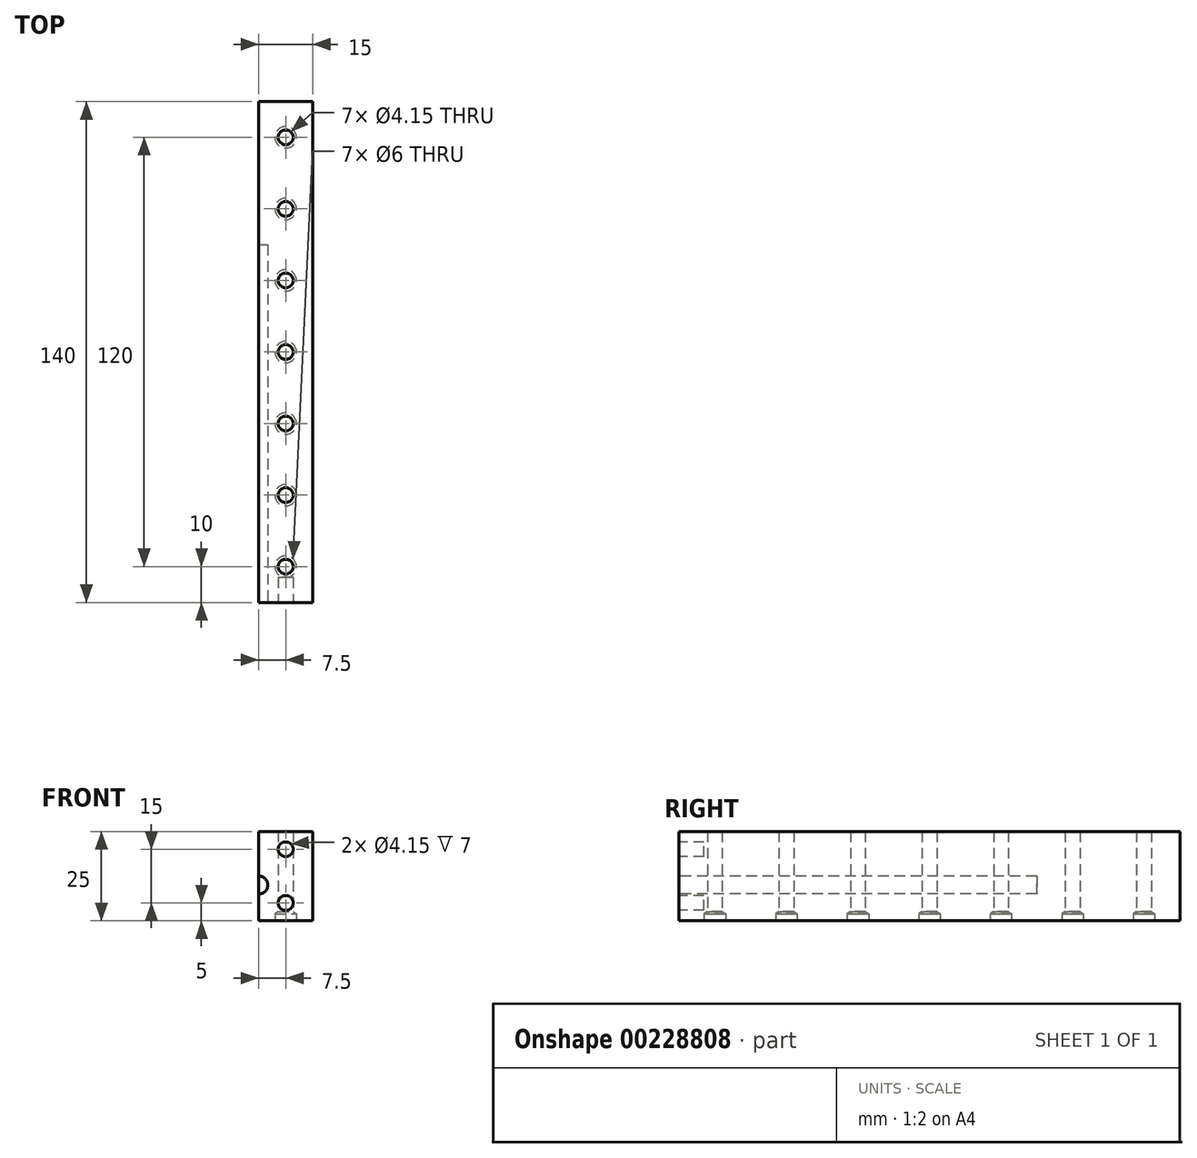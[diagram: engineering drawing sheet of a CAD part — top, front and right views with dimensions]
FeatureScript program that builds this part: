
annotation { "Feature Type Name" : "Feature", "Feature Type Description" : "" }
export const myFeature = defineFeature(function(context is Context, id is Id, definition is map)
    precondition{}
    {
        {
            var Q0;
            Q0=qCreatedBy(makeId("Top.planeOp"),FACE);
            var sketch = newSketch(context, id + "F0", { "sketchPlane" : qUnion([Q0])});
            skLineSegment(sketch, "E0.bottom", {"start": v(-7.5, 90) * mm, "end": v(7.5, 90) * mm});
            skLineSegment(sketch, "E0.top", {"start": v(-7.5, -50) * mm, "end": v(7.5, -50) * mm});
            skLineSegment(sketch, "E0.left", {"start": v(-7.5, 90) * mm, "end": v(-7.5, -50) * mm});
            skLineSegment(sketch, "E0.right", {"start": v(7.5, 90) * mm, "end": v(7.5, -50) * mm});
            skCircle(sketch, "E1", {"center": v(0, -40) * mm, "radius": 2.07 * mm});
            skCircle(sketch, "E2.0.1.0", {"center": v(0, -20) * mm, "radius": 2.07 * mm});
            skCircle(sketch, "E2.0.2.0", {"center": v(0, 0) * mm, "radius": 2.07 * mm});
            skCircle(sketch, "E2.0.3.0", {"center": v(0, 20) * mm, "radius": 2.07 * mm});
            skCircle(sketch, "E2.0.4.0", {"center": v(0, 40) * mm, "radius": 2.07 * mm});
            skLineSegment(sketch, "E2.direction1", {"start": v(0, -40) * mm, "end": v(25, -40) * mm, "construction": true});
            skLineSegment(sketch, "E2.direction2", {"start": v(0, -40) * mm, "end": v(0, -20) * mm, "construction": true});
            skCircle(sketch, "E3.0.0.5", {"center": v(0, 60) * mm, "radius": 2.07 * mm});
            skCircle(sketch, "E3.0.0.6", {"center": v(0, 80) * mm, "radius": 2.07 * mm});
            skSolve(sketch);
        }
        {
            var Q0;
            Q0=makeQuery(id+"F0.imprint","IMPRINT",FACE,{"disambiguationData":[TD([[makeQuery(id+"F0.imprint","IMPRINT",EDGE,{"derivedFrom":sQuery(id+"F0.wireOp",EDGE,"E0.bottom")}),-1.0]])]});
            extrude(context, id + "F1", {"entities" : qUnion([Q0]), "depth" : 25 * mm});
        }
        {
            var Q0;
            Q0=makeQuery(id+"F1.opExtrude","SWEPT_FACE",FACE,{"disambiguationData":[OSD([sQuery(id+"F0.wireOp",EDGE,"E0.top")])]});
            var sketch = newSketch(context, id + "F2", { "sketchPlane" : qUnion([Q0])});
            skCircle(sketch, "E4", {"center": v(-7.5, 10) * mm, "radius": 2.5 * mm});
            skSolve(sketch);
        }
        {
            var Q0;
            {var subQ0=sQuery(id+"F2.wireOp",EDGE,"E4");var subQ1=makeQuery(id+"F1.opExtrude","SWEPT_EDGE",EDGE,{"disambiguationData":[OSD([sQuery(id+"F0.wireOp",EDGE,"E0.top"),sQuery(id+"F0.wireOp",EDGE,"E0.left")])]});var subQ2=makeQuery(id+"F2.imprint","INTERSECT",VERTEX,{"disambiguationData":[OD(0.0)],"derivedFrom":[subQ1,subQ0]});Q0=makeQuery(id+"F2.imprint","IMPRINT",FACE,{"disambiguationData":[TD([[makeQuery(id+"F2.imprint","IMPRINT",EDGE,{"disambiguationData":[TD([[subQ2,1.0]])],"derivedFrom":subQ0}),1.0]])]});}
            var Q1;
            {var subQ0=sQuery(id+"F2.wireOp",EDGE,"E4");var subQ1=makeQuery(id+"F1.opExtrude","SWEPT_EDGE",EDGE,{"disambiguationData":[OSD([sQuery(id+"F0.wireOp",EDGE,"E0.top"),sQuery(id+"F0.wireOp",EDGE,"E0.left")])]});var subQ2=makeQuery(id+"F2.imprint","INTERSECT",VERTEX,{"disambiguationData":[OD(0.0)],"derivedFrom":[subQ1,subQ0]});Q1=makeQuery(id+"F2.imprint","IMPRINT",FACE,{"disambiguationData":[TD([[makeQuery(id+"F2.imprint","IMPRINT",EDGE,{"disambiguationData":[TD([[subQ2,-1.0]])],"derivedFrom":subQ0}),1.0]])]});}
            var Q2;
            Q2=makeQuery(id+"F1.opExtrude","SWEPT_FACE",FACE,{"disambiguationData":[OSD([sQuery(id+"F0.wireOp",EDGE,"E0.bottom")])]});
            extrude(context, id + "F3", {"entities" : qUnion([Q0, Q1]), "operationType" : NewBodyOperationType.REMOVE, "oppositeDirection" : true, "endBoundEntityFace" : qUnion([Q2]), "depth" : 100 * mm});
        }
        {
            var Q0;
            Q0=sQuery(id+"F0.wireOp",VERTEX,"E1.center");
            var Q1;
            Q1=sQuery(id+"F0.wireOp",VERTEX,"E2.direction2.end");
            var Q2;
            Q2=sQuery(id+"F0.wireOp",VERTEX,"E2.0.2.0.center");
            var Q3;
            Q3=sQuery(id+"F0.wireOp",VERTEX,"E2.0.3.0.center");
            var Q4;
            Q4=sQuery(id+"F0.wireOp",VERTEX,"E2.0.4.0.center");
            var Q5;
            Q5=sQuery(id+"F0.wireOp",VERTEX,"E3.0.0.5.center");
            var Q6;
            Q6=sQuery(id+"F0.wireOp",VERTEX,"E3.0.0.6.center");
            var Q7;
            Q7=makeQuery(id+"F1.opExtrude","SWEPT_BODY",BODY,{"disambiguationData":[OSD([sQuery(id+"F0.wireOp",EDGE,"E0.bottom"),sQuery(id+"F0.wireOp",EDGE,"E0.top"),sQuery(id+"F0.wireOp",EDGE,"E0.left"),sQuery(id+"F0.wireOp",EDGE,"E0.right"),sQuery(id+"F0.wireOp",EDGE,"E1"),sQuery(id+"F0.wireOp",EDGE,"E2.0.1.0"),sQuery(id+"F0.wireOp",EDGE,"E2.0.2.0"),sQuery(id+"F0.wireOp",EDGE,"E2.0.3.0"),sQuery(id+"F0.wireOp",EDGE,"E2.0.4.0")])]});
            hole(context, id + "F4", {"style" : HoleStyle.SIMPLE, "endStyle" : HoleEndStyle.BLIND, "oppositeDirection" : true, "holeDiameter" : 6 * mm, "holeDepth" : 2 * mm, "locations" : qUnion([Q0, Q1, Q2, Q3, Q4, Q5, Q6]), "scope" : qUnion([Q7]), "tappedDepth" : 12 * mm, "tapClearance" : 3});
        }
        {
            var Q0;
            Q0=makeQuery(id+"F1.opExtrude","SWEPT_FACE",FACE,{"disambiguationData":[OSD([sQuery(id+"F0.wireOp",EDGE,"E0.top")])]});
            var sketch = newSketch(context, id + "F5", { "sketchPlane" : qUnion([Q0])});
            skSolve(sketch);
        }
        {
            var Q0;
            {var subQ7=sQuery(id+"F0.wireOp",EDGE,"E0.top");Q0=makeQuery(id+"F5.imprint","IMPRINT",FACE,{"disambiguationData":[TD([[makeQuery(id+"F5.imprint","IMPRINT",EDGE,{"derivedFrom":makeQuery(id+"F1.opExtrude","CAP_EDGE",EDGE,{"disambiguationData":[OSD([subQ7])],"isStart":true})}),1.0]])]});}
            var sketch = newSketch(context, id + "F6", { "sketchPlane" : qUnion([Q0])});
            skCircle(sketch, "E5", {"center": v(0, 5) * mm, "radius": 2.07 * mm});
            skLineSegment(sketch, "E6", {"start": v(0, 25) * mm, "end": v(0, 0) * mm, "construction": true});
            skLineSegment(sketch, "E7", {"start": v(0, 12.5) * mm, "end": v(-7.5, 12.5) * mm, "construction": true});
            skCircle(sketch, "E8.MirrorC", {"center": v(0, 20) * mm, "radius": 2.07 * mm});
            skSolve(sketch);
        }
        {
            var Q0;
            Q0 = qSketchRegion(id + "F6", true);
            extrude(context, id + "F7", {"entities" : qUnion([Q0]), "operationType" : NewBodyOperationType.REMOVE, "oppositeDirection" : true, "depth" : 7 * mm});
        }
    });
